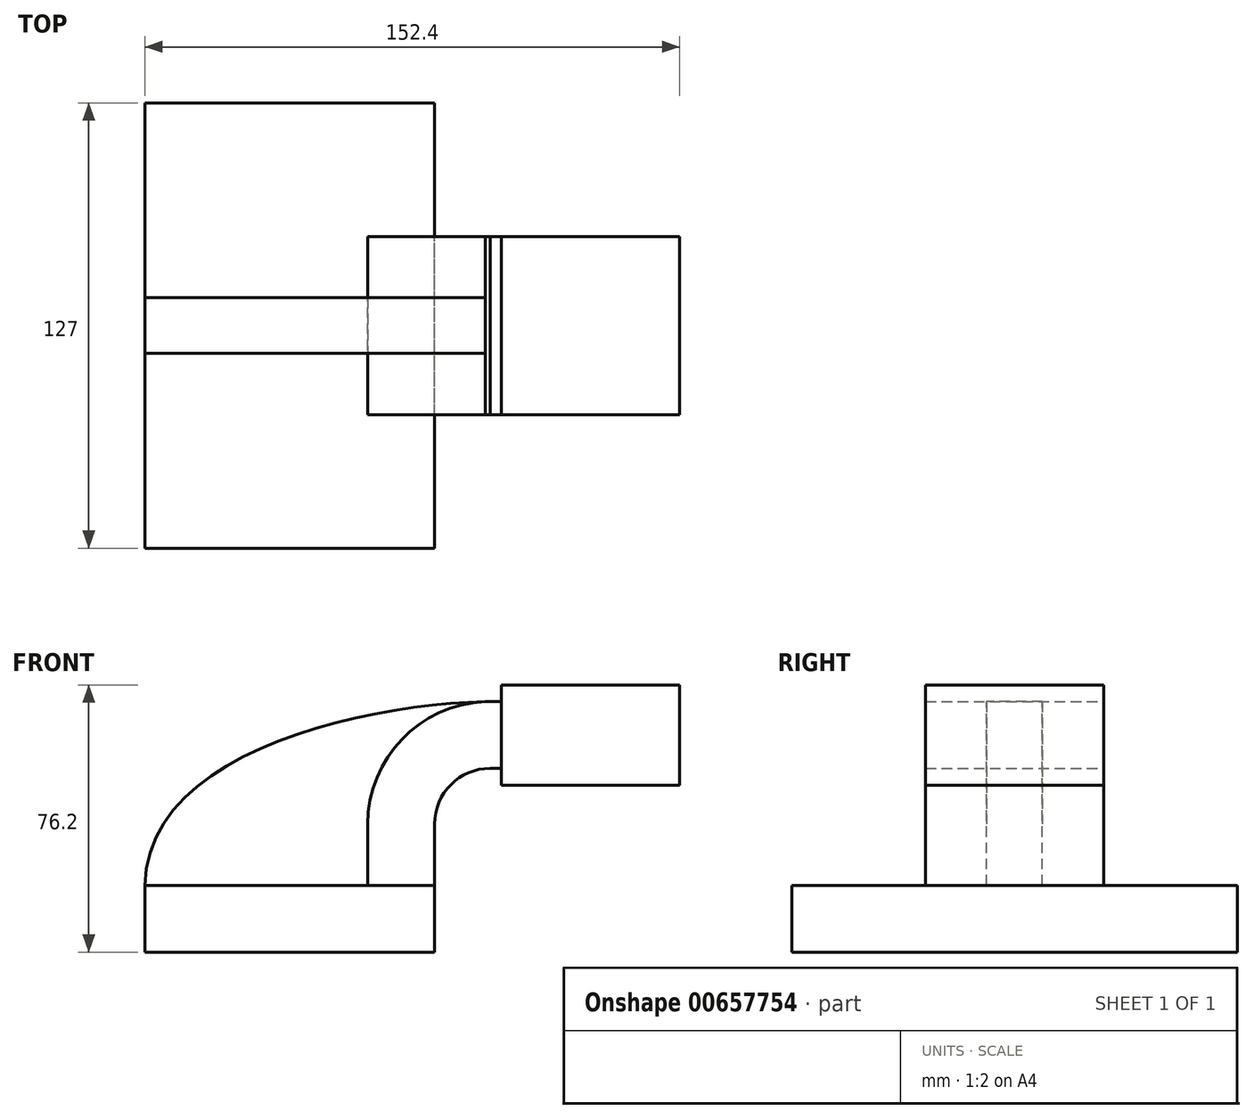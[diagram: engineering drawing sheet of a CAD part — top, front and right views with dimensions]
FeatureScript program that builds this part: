
annotation { "Feature Type Name" : "Feature", "Feature Type Description" : "" }
export const myFeature = defineFeature(function(context is Context, id is Id, definition is map)
    precondition{}
    {
        {
            var Q0;
            Q0=qCreatedBy(makeId("Front.planeOp"),FACE);
            var sketch = newSketch(context, id + "F0", { "sketchPlane" : qUnion([Q0])});
            skLineSegment(sketch, "E0.bottom", {"start": v(-41.28, 9.52) * mm, "end": v(41.27, 9.53) * mm});
            skLineSegment(sketch, "E0.top", {"start": v(-41.28, -9.53) * mm, "end": v(41.28, -9.53) * mm});
            skLineSegment(sketch, "E0.left", {"start": v(-41.28, 9.52) * mm, "end": v(-41.27, -9.53) * mm});
            skLineSegment(sketch, "E0.right", {"start": v(41.28, 9.53) * mm, "end": v(41.28, -9.52) * mm});
            skPoint(sketch, "E0.middle", {"position": v(0, 0) * mm});
            skLineSegment(sketch, "E1.bottom", {"start": v(60.33, 38.1) * mm, "end": v(111.13, 38.1) * mm});
            skLineSegment(sketch, "E1.top", {"start": v(60.32, 66.67) * mm, "end": v(111.12, 66.67) * mm});
            skLineSegment(sketch, "E1.left", {"start": v(60.33, 38.1) * mm, "end": v(60.32, 66.67) * mm});
            skLineSegment(sketch, "E1.right", {"start": v(111.13, 38.1) * mm, "end": v(111.12, 66.67) * mm});
            skLineSegment(sketch, "E2", {"start": v(41.27, 9.53) * mm, "end": v(41.27, 27) * mm});
            skArc(sketch, "E3", {"start": v(41.28, 27) * mm, "mid": v(45.92, 38.23) * mm, "end": v(57.15, 42.88) * mm});
            skLineSegment(sketch, "E4", {"start": v(57.15, 42.88) * mm, "end": v(89.26, 42.88) * mm});
            skLineSegment(sketch, "E5.0", {"start": v(57.15, 61.93) * mm, "end": v(89.26, 61.93) * mm});
            skArc(sketch, "E5.1", {"start": v(22.23, 27) * mm, "mid": v(32.45, 51.7) * mm, "end": v(57.15, 61.93) * mm});
            skLineSegment(sketch, "E5.2", {"start": v(22.23, 9.53) * mm, "end": v(22.23, 27) * mm});
            skLineSegment(sketch, "E6", {"start": v(89.26, 38.1) * mm, "end": v(89.26, 66.67) * mm});
            skFitSpline(sketch, "E7", {"points": [v(-41.28, 9.53) * mm, v(57.15, 61.93) * mm], "startDerivative": vector(1.87, 115.3) * mm, "endDerivative": vector(106.13, 1.7) * mm});
            skSolve(sketch);
        }
        {
            var Q0;
            Q0=makeQuery(id+"F0.imprint","IMPRINT",FACE,{"disambiguationData":[TD([[makeQuery(id+"F0.imprint","IMPRINT",EDGE,{"derivedFrom":sQuery(id+"F0.wireOp",EDGE,"E0.top")}),1.0]])]});
            extrude(context, id + "F1", {"entities" : qUnion([Q0]), "endBound" : BoundingType.SYMMETRIC, "depth" : 127 * mm, "offsetDistance" : 25.4 * mm});
        }
        {
            var Q0;
            {var subQ1=sQuery(id+"F0.wireOp",EDGE,"E2");Q0=makeQuery(id+"F0.imprint","IMPRINT",FACE,{"disambiguationData":[TD([[makeQuery(id+"F0.imprint","IMPRINT",EDGE,{"derivedFrom":subQ1}),1.0]])]});}
            extrude(context, id + "F2", {"entities" : qUnion([Q0]), "endBound" : BoundingType.SYMMETRIC, "depth" : 50.8 * mm, "offsetDistance" : 25.4 * mm});
        }
        {
            var Q0;
            {var subQ0=sQuery(id+"F0.wireOp",EDGE,"E1.left");var subQ1=sQuery(id+"F0.wireOp",EDGE,"E1.top");var subQ2=makeQuery(id+"F0.imprint","INTERSECT",VERTEX,{"derivedFrom":[subQ1,subQ0]});Q0=makeQuery(id+"F0.imprint","IMPRINT",FACE,{"disambiguationData":[TD([[makeQuery(id+"F0.imprint","IMPRINT",EDGE,{"disambiguationData":[TD([[subQ2,-1.0]])],"derivedFrom":subQ1}),-1.0]])]});}
            var Q1;
            {var subQ0=sQuery(id+"F0.wireOp",EDGE,"E4");var subQ1=sQuery(id+"F0.wireOp",EDGE,"E1.left");var subQ2=makeQuery(id+"F0.imprint","INTERSECT",VERTEX,{"derivedFrom":[subQ1,subQ0]});Q1=makeQuery(id+"F0.imprint","IMPRINT",FACE,{"disambiguationData":[TD([[makeQuery(id+"F0.imprint","IMPRINT",EDGE,{"disambiguationData":[TD([[subQ2,-1.0]])],"derivedFrom":subQ1}),-1.0]])]});}
            var Q2;
            {var subQ4=sQuery(id+"F0.wireOp",EDGE,"E1.right");Q2=makeQuery(id+"F0.imprint","IMPRINT",FACE,{"disambiguationData":[TD([[makeQuery(id+"F0.imprint","IMPRINT",EDGE,{"derivedFrom":subQ4}),1.0]])]});}
            var Q3;
            {var subQ0=sQuery(id+"F0.wireOp",EDGE,"E1.left");var subQ1=sQuery(id+"F0.wireOp",EDGE,"E1.bottom");var subQ2=makeQuery(id+"F0.imprint","INTERSECT",VERTEX,{"derivedFrom":[subQ1,subQ0]});Q3=makeQuery(id+"F0.imprint","IMPRINT",FACE,{"disambiguationData":[TD([[makeQuery(id+"F0.imprint","IMPRINT",EDGE,{"disambiguationData":[TD([[subQ2,-1.0]])],"derivedFrom":subQ1}),1.0]])]});}
            extrude(context, id + "F3", {"entities" : qUnion([Q0, Q1, Q2, Q3]), "endBound" : BoundingType.SYMMETRIC, "depth" : 50.8 * mm, "offsetDistance" : 25.4 * mm});
        }
        {
            var Q0;
            {var subQ3=sQuery(id+"F0.wireOp",EDGE,"E5.2");Q0=makeQuery(id+"F0.imprint","IMPRINT",FACE,{"disambiguationData":[TD([[makeQuery(id+"F0.imprint","IMPRINT",EDGE,{"derivedFrom":subQ3}),1.0]])]});}
            extrude(context, id + "F4", {"entities" : qUnion([Q0]), "endBound" : BoundingType.SYMMETRIC, "oppositeDirection" : true, "depth" : 15.88 * mm, "offsetDistance" : 25.4 * mm});
        }
    });
